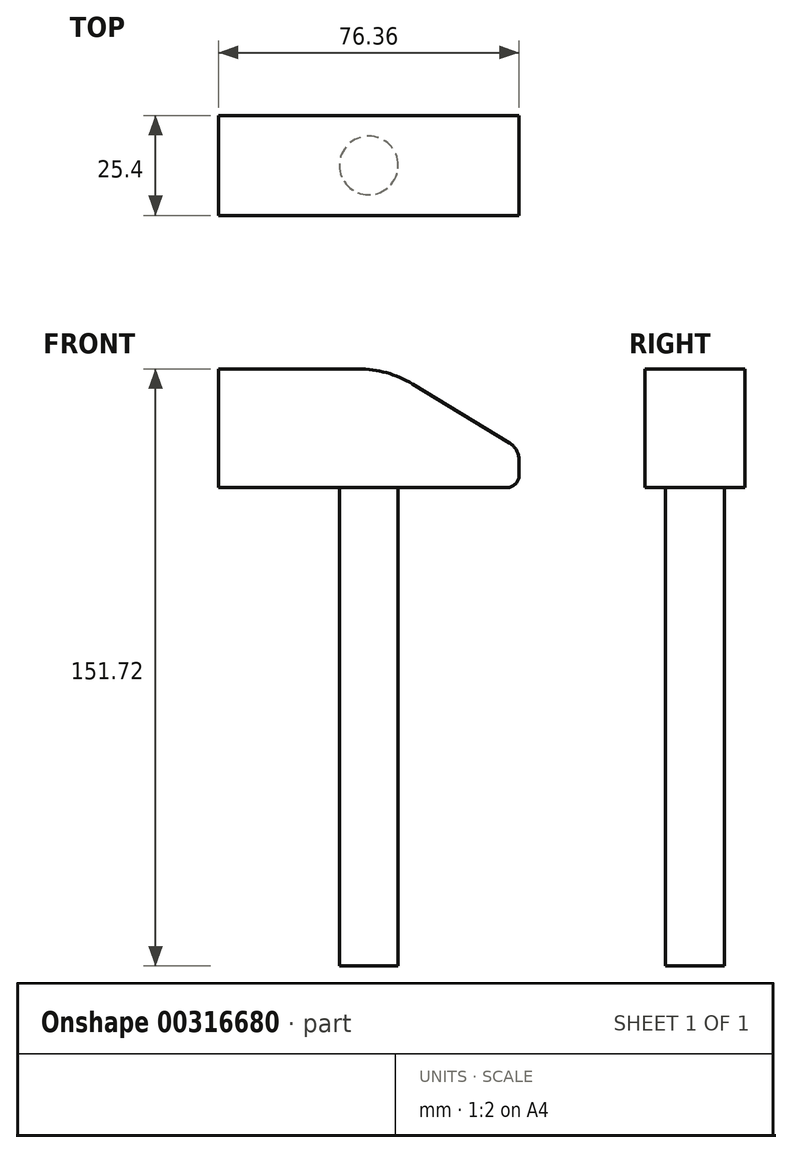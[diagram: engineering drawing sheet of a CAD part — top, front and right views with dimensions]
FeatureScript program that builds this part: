
annotation { "Feature Type Name" : "Feature", "Feature Type Description" : "" }
export const myFeature = defineFeature(function(context is Context, id is Id, definition is map)
    precondition{}
    {
        {
            var Q0;
            Q0=qCreatedBy(makeId("Front.planeOp"),FACE);
            var sketch = newSketch(context, id + "F0", { "sketchPlane" : qUnion([Q0])});
            skLineSegment(sketch, "E0.bottom", {"start": v(4.78, 15.07) * mm, "end": v(-38.18, 15.07) * mm});
            skLineSegment(sketch, "E0.top", {"start": v(38.18, -15.07) * mm, "end": v(-38.18, -15.07) * mm});
            skLineSegment(sketch, "E0.left", {"start": v(38.18, -5.21) * mm, "end": v(38.18, -15.07) * mm});
            skLineSegment(sketch, "E0.right", {"start": v(-38.18, 15.07) * mm, "end": v(-38.18, -15.07) * mm});
            skPoint(sketch, "E0.middle", {"position": v(0, 0) * mm});
            skLineSegment(sketch, "E1", {"start": v(38.18, -5.21) * mm, "end": v(4.78, 15.07) * mm});
            skPoint(sketch, "E2.orphan", {"position": v(38.18, 15.07) * mm});
            skSolve(sketch);
        }
        {
            var Q0;
            Q0 = qSketchRegion(id + "F0", true);
            extrude(context, id + "F1", {"entities" : qUnion([Q0]), "endBound" : BoundingType.SYMMETRIC, "depth" : 25.4 * mm});
        }
        {
            var Q0;
            Q0=qCreatedBy(makeId("Top.planeOp"),FACE);
            var sketch = newSketch(context, id + "F2", { "sketchPlane" : qUnion([Q0])});
            skCircle(sketch, "E3", {"center": v(0, 0) * mm, "radius": 7.46 * mm});
            skSolve(sketch);
        }
        {
            var Q0;
            Q0 = qSketchRegion(id + "F2", true);
            extrude(context, id + "F3", {"entities" : qUnion([Q0]), "operationType" : NewBodyOperationType.ADD, "oppositeDirection" : true, "depth" : 136.65 * mm});
        }
        {
            var Q0;
            Q0=makeQuery(id+"F1.opExtrude","SWEPT_EDGE",EDGE,{"disambiguationData":[OSD([sQuery(id+"F0.wireOp",EDGE,"E0.left"),sQuery(id+"F0.wireOp",EDGE,"E1")])]});
            fillet(context, id + "F4", {"entities" : qUnion([Q0]), "radius" : 5.17 * mm, "tangentPropagation" : true, "allowEdgeOverflow" : false});
        }
        {
            var Q0;
            Q0=makeQuery(id+"F1.opExtrude","SWEPT_EDGE",EDGE,{"disambiguationData":[OSD([sQuery(id+"F0.wireOp",EDGE,"E0.top"),sQuery(id+"F0.wireOp",EDGE,"E0.left")])]});
            fillet(context, id + "F5", {"entities" : qUnion([Q0]), "radius" : 3.07 * mm, "tangentPropagation" : true, "allowEdgeOverflow" : false});
        }
        {
            var Q0;
            Q0=makeQuery(id+"F1.opExtrude","SWEPT_EDGE",EDGE,{"disambiguationData":[OSD([sQuery(id+"F0.wireOp",EDGE,"E0.bottom"),sQuery(id+"F0.wireOp",EDGE,"E1")])]});
            fillet(context, id + "F6", {"entities" : qUnion([Q0]), "radius" : 26.45 * mm, "tangentPropagation" : true, "allowEdgeOverflow" : false});
        }
    });
